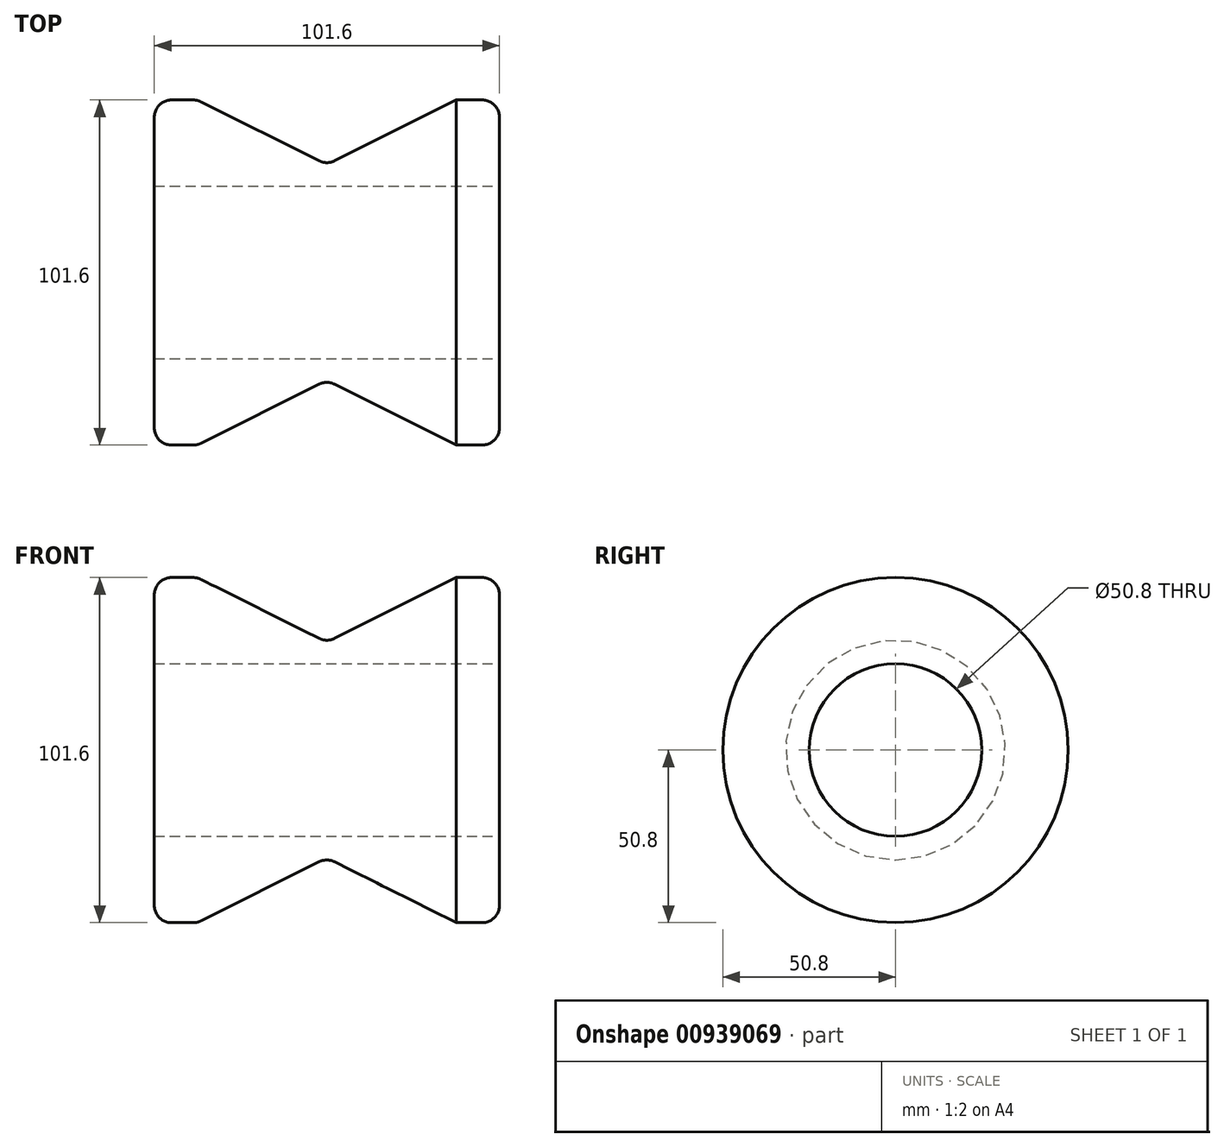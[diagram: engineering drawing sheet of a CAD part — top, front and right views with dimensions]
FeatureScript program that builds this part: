
annotation { "Feature Type Name" : "Feature", "Feature Type Description" : "" }
export const myFeature = defineFeature(function(context is Context, id is Id, definition is map)
    precondition{}
    {
        {
            var Q0;
            Q0=qCreatedBy(makeId("Right.planeOp"),FACE);
            var sketch = newSketch(context, id + "F0", { "sketchPlane" : qUnion([Q0])});
            skCircle(sketch, "E0", {"center": v(0, 0) * mm, "radius": 50.8 * mm});
            skSolve(sketch);
        }
        {
            var Q0;
            Q0 = qSketchRegion(id + "F0", true);
            extrude(context, id + "F1", {"entities" : qUnion([Q0]), "endBound" : BoundingType.SYMMETRIC, "depth" : 101.6 * mm, "offsetDistance" : 25.4 * mm});
        }
        {
            var Q0;
            Q0=makeQuery(id+"F1.opExtrude","CAP_FACE",FACE,{"disambiguationData":[OSD([sQuery(id+"F0.wireOp",EDGE,"E0")])],"isStart":false});
            var sketch = newSketch(context, id + "F2", { "sketchPlane" : qUnion([Q0])});
            skCircle(sketch, "E1", {"center": v(0, 0) * mm, "radius": 25.4 * mm});
            skSolve(sketch);
        }
        {
            var Q0;
            Q0 = qSketchRegion(id + "F2", true);
            extrude(context, id + "F3", {"entities" : qUnion([Q0]), "operationType" : NewBodyOperationType.REMOVE, "endBound" : BoundingType.THROUGH_ALL, "oppositeDirection" : true, "depth" : 25.4 * mm, "offsetDistance" : 25.4 * mm});
        }
        {
            var Q0;
            Q0=qCreatedBy(makeId("Front.planeOp"),FACE);
            var sketch = newSketch(context, id + "F4", { "sketchPlane" : qUnion([Q0])});
            skLineSegment(sketch, "E2", {"start": v(-111.74, 0) * mm, "end": v(103.19, 0) * mm, "construction": true});
            skLineSegment(sketch, "E3", {"start": v(-38.1, 50.8) * mm, "end": v(0, 31.75) * mm});
            skLineSegment(sketch, "E4", {"start": v(0, 31.75) * mm, "end": v(38.1, 50.8) * mm});
            skLineSegment(sketch, "E5", {"start": v(38.1, 50.8) * mm, "end": v(-38.1, 50.8) * mm});
            skSolve(sketch);
        }
        {
            var Q0;
            Q0 = qSketchRegion(id + "F4", true);
            var Q1;
            Q1=sQuery(id+"F4.wireOp",EDGE,"E2");
            revolve(context, id + "F5", {"operationType" : NewBodyOperationType.REMOVE, "surfaceOperationType" : NewSurfaceOperationType.NEW, "entities" : qUnion([Q0]), "axis" : qUnion([Q1]), "revolveType" : RevolveType.FULL, "oppositeDirection" : true});
        }
        {
            var Q0;
            Q0=makeQuery(id+"F5.boolean.opBoolean","COPY",EDGE,{"derivedFrom":makeQuery(id+"F5.opRevolve","SWEPT_EDGE",EDGE,{"disambiguationData":[OSD([sQuery(id+"F4.wireOp",EDGE,"E3"),sQuery(id+"F4.wireOp",EDGE,"E4")])]})});
            fillet(context, id + "F6", {"entities" : qUnion([Q0]), "radius" : 5.08 * mm, "tangentPropagation" : true, "allowEdgeOverflow" : false});
        }
        {
            var Q0;
            Q0=makeQuery(id+"F5.boolean.opBoolean","COPY",EDGE,{"derivedFrom":makeQuery(id+"F5.opRevolve","SWEPT_EDGE",EDGE,{"disambiguationData":[OSD([sQuery(id+"F4.wireOp",EDGE,"E4"),sQuery(id+"F4.wireOp",EDGE,"E5")])]})});
            var Q1;
            Q1=makeQuery(id+"F1.opExtrude","CAP_EDGE",EDGE,{"disambiguationData":[OSD([sQuery(id+"F0.wireOp",EDGE,"E0")])],"isStart":false});
            var Q2;
            Q2=makeQuery(id+"F5.boolean.opBoolean","COPY",EDGE,{"derivedFrom":makeQuery(id+"F5.opRevolve","SWEPT_EDGE",EDGE,{"disambiguationData":[OSD([sQuery(id+"F4.wireOp",EDGE,"E3"),sQuery(id+"F4.wireOp",EDGE,"E5")])]})});
            var Q3;
            Q3=makeQuery(id+"F1.opExtrude","CAP_EDGE",EDGE,{"disambiguationData":[OSD([sQuery(id+"F0.wireOp",EDGE,"E0")])],"isStart":true});
            fillet(context, id + "F7", {"entities" : qUnion([Q0, Q1, Q2, Q3]), "radius" : 5.08 * mm, "tangentPropagation" : true, "allowEdgeOverflow" : false});
        }
    });
